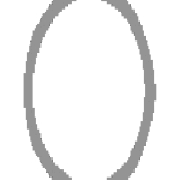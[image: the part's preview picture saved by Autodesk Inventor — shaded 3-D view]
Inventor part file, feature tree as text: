
AUTODESK INVENTOR PART (.ipt)
format: ipt  version: 2021 (Build 250183000, 183)  size: 109,568 bytes
history: native  units: in
note: dims shown in document units (in); Inventor stores cm internally (conversion verified against a paired STEP export)
features: other x4, sketch x3, plane x1
ambient origin geometry x8: Origin, YZ Plane, XZ Plane, XY Plane, X Axis, Y Axis, Z Axis, Center Point
bodies: Solid1 (feature_tree), Body (feature_tree)
feature tree (8):
  other  "Driven Length"
  other  "Frame Generator"
  other  "Start Plane"
  other  "End Plane"
  sketch  "Sketch"  dims[d2=15.5in d4=-0.0in d5=15.5in d6=0.12in d7=0.0in d8=90.0deg d9=15.5in]
  sketch  "Sketch2"  dims[d0=1.0in]
  plane  "Work Plane3"
  sketch  "Sketch3"  dims[d1=0.065in]
